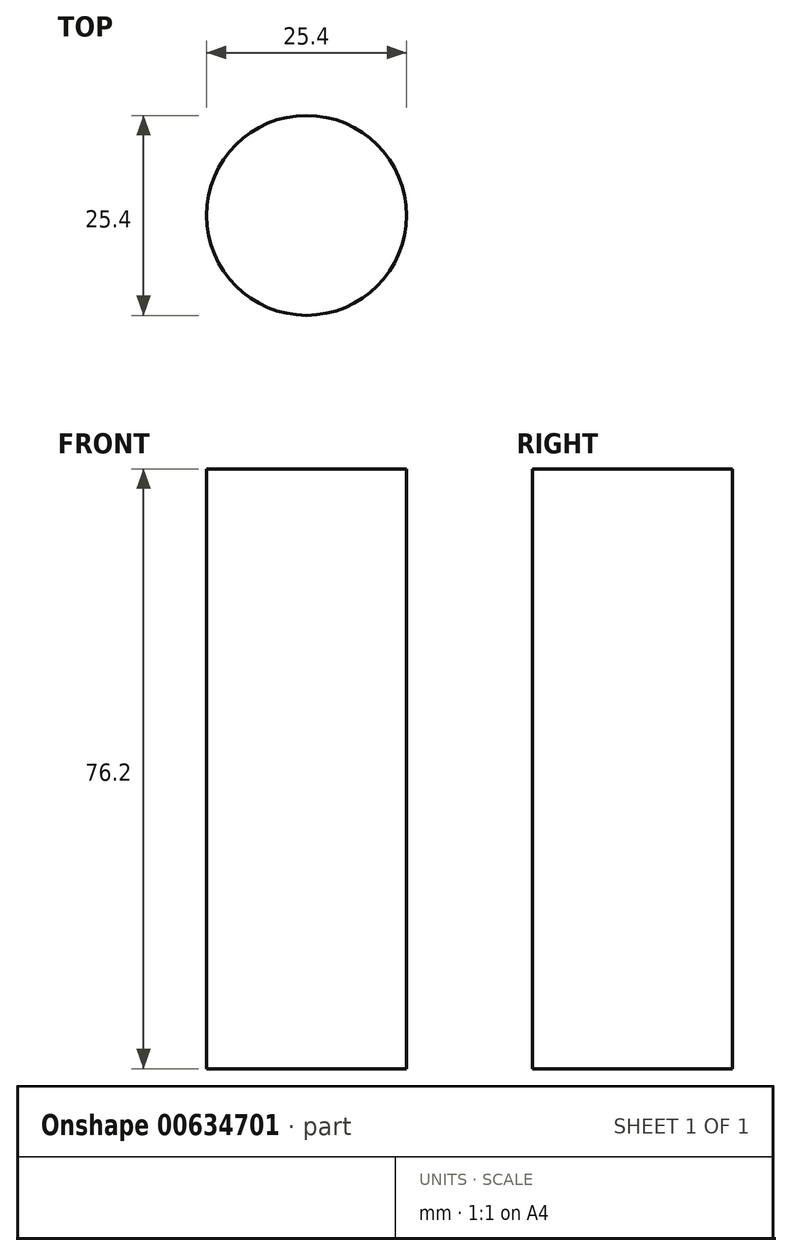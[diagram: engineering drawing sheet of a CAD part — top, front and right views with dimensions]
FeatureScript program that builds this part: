
annotation { "Feature Type Name" : "Feature", "Feature Type Description" : "" }
export const myFeature = defineFeature(function(context is Context, id is Id, definition is map)
    precondition{}
    {
        {
            assignVariable(context, id + "F0", {"name" : "high", "anyValue" : 76.2 * mm});
        }
        {
            var Q0;
            Q0=qCreatedBy(makeId("Top.planeOp"),FACE);
            var sketch = newSketch(context, id + "F1", { "sketchPlane" : qUnion([Q0])});
            skCircle(sketch, "E0", {"center": v(0, 0) * mm, "radius": 12.7 * mm});
            skSolve(sketch);
        }
        {
            var Q0;
            Q0=sQuery(id+"F1.wireOp",EDGE,"E0");
            extrude(context, id + "F2", {"bodyType" : ToolBodyType.SURFACE, "surfaceEntities" : qUnion([Q0]), "depth" : getVariable(context, 'high'), "offsetDistance" : 25.4 * mm});
        }
    });
